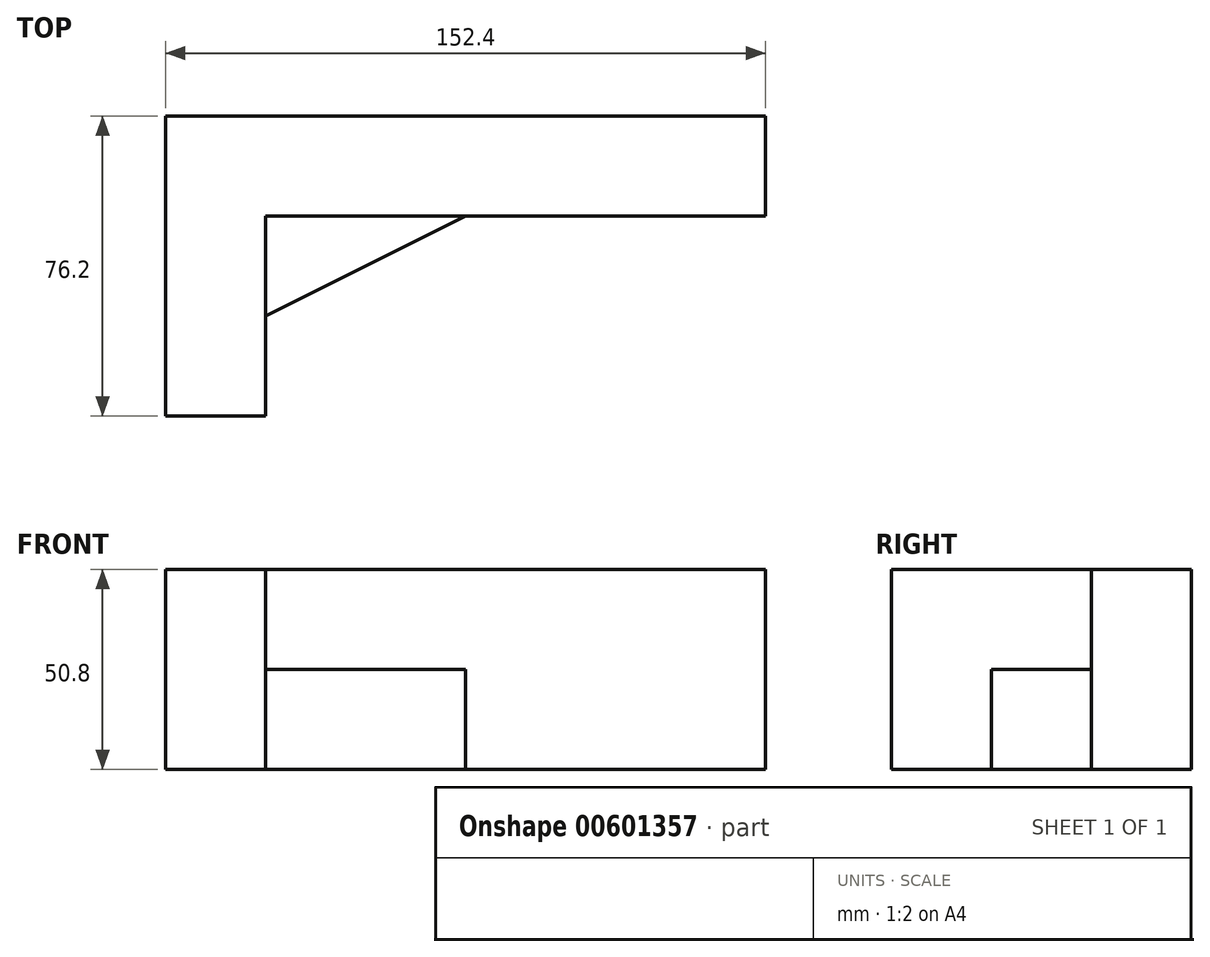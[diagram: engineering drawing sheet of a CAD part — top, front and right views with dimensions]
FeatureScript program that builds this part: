
annotation { "Feature Type Name" : "Feature", "Feature Type Description" : "" }
export const myFeature = defineFeature(function(context is Context, id is Id, definition is map)
    precondition{}
    {
        {
            var Q0;
            Q0=qCreatedBy(makeId("Front.planeOp"),FACE);
            var sketch = newSketch(context, id + "F0", { "sketchPlane" : qUnion([Q0])});
            skLineSegment(sketch, "E0", {"start": v(0, 0) * mm, "end": v(0, 50.8) * mm});
            skLineSegment(sketch, "E1", {"start": v(0, 50.8) * mm, "end": v(152.4, 50.8) * mm});
            skLineSegment(sketch, "E2", {"start": v(152.4, 50.8) * mm, "end": v(152.4, 0) * mm});
            skLineSegment(sketch, "E3", {"start": v(152.4, 0) * mm, "end": v(0, 0) * mm});
            skSolve(sketch);
        }
        {
            var Q0;
            Q0 = qSketchRegion(id + "F0", true);
            extrude(context, id + "F1", {"entities" : qUnion([Q0]), "oppositeDirection" : true, "depth" : 76.2 * mm, "offsetDistance" : 25.4 * mm});
        }
        {
            var Q0;
            Q0=makeQuery(id+"F1.opExtrude","SWEPT_FACE",FACE,{"disambiguationData":[OSD([sQuery(id+"F0.wireOp",EDGE,"E1")])]});
            var sketch = newSketch(context, id + "F2", { "sketchPlane" : qUnion([Q0])});
            skLineSegment(sketch, "E4", {"start": v(25.4, 0) * mm, "end": v(25.4, 50.8) * mm});
            skLineSegment(sketch, "E5", {"start": v(25.4, 50.8) * mm, "end": v(152.4, 50.8) * mm});
            skSolve(sketch);
        }
        {
            var Q0;
            Q0 = qSketchRegion(id + "F2", true);
            var Q1;
            {var subQ0=sQuery(id+"F2.wireOp",EDGE,"E4");Q1=makeQuery(id+"F2.imprint","IMPRINT",FACE,{"disambiguationData":[TD([[makeQuery(id+"F2.imprint","IMPRINT",EDGE,{"derivedFrom":subQ0}),-1.0]])]});}
            extrude(context, id + "F3", {"entities" : qUnion([Q0, Q1]), "operationType" : NewBodyOperationType.REMOVE, "oppositeDirection" : true, "depth" : 50.8 * mm, "offsetDistance" : 25.4 * mm});
        }
        {
            var Q0;
            Q0=makeQuery(id+"F1.opExtrude","SWEPT_FACE",FACE,{"disambiguationData":[OSD([sQuery(id+"F0.wireOp",EDGE,"E3")])]});
            var sketch = newSketch(context, id + "F4", { "sketchPlane" : qUnion([Q0])});
            skLineSegment(sketch, "E6", {"start": v(25.4, -50.8) * mm, "end": v(25.4, -25.4) * mm});
            skLineSegment(sketch, "E7", {"start": v(25.4, -25.4) * mm, "end": v(76.2, -50.8) * mm});
            skLineSegment(sketch, "E8", {"start": v(76.2, -50.8) * mm, "end": v(25.4, -50.8) * mm});
            skSolve(sketch);
        }
        {
            var Q0;
            Q0=makeQuery(id+"F4.imprint","IMPRINT",FACE,{"disambiguationData":[TD([[makeQuery(id+"F4.imprint","IMPRINT",EDGE,{"derivedFrom":sQuery(id+"F4.wireOp",EDGE,"E6")}),1.0]])]});
            extrude(context, id + "F5", {"entities" : qUnion([Q0]), "operationType" : NewBodyOperationType.ADD, "oppositeDirection" : true, "depth" : 25.4 * mm, "offsetDistance" : 25.4 * mm});
        }
    });
